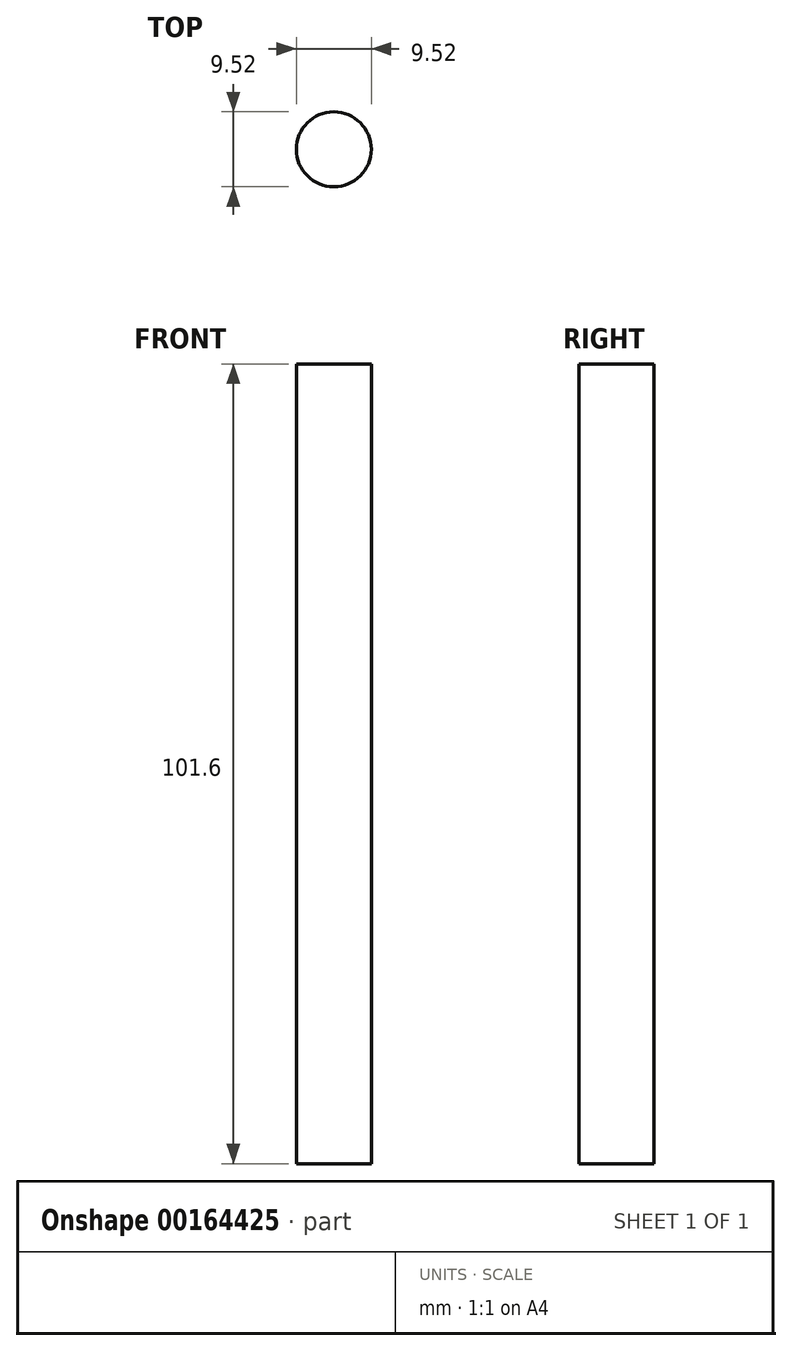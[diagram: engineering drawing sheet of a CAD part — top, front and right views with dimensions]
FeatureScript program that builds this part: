
annotation { "Feature Type Name" : "Feature", "Feature Type Description" : "" }
export const myFeature = defineFeature(function(context is Context, id is Id, definition is map)
    precondition{}
    {
        {
            var Q0;
            Q0=qCreatedBy(makeId("Top.planeOp"),FACE);
            var sketch = newSketch(context, id + "F0", { "sketchPlane" : qUnion([Q0])});
            skCircle(sketch, "E0", {"center": v(0, 0) * mm, "radius": 4.76 * mm});
            skSolve(sketch);
        }
        {
            var Q0;
            Q0 = qSketchRegion(id + "F0", true);
            extrude(context, id + "F1", {"entities" : qUnion([Q0]), "depth" : 101.6 * mm});
        }
    });
